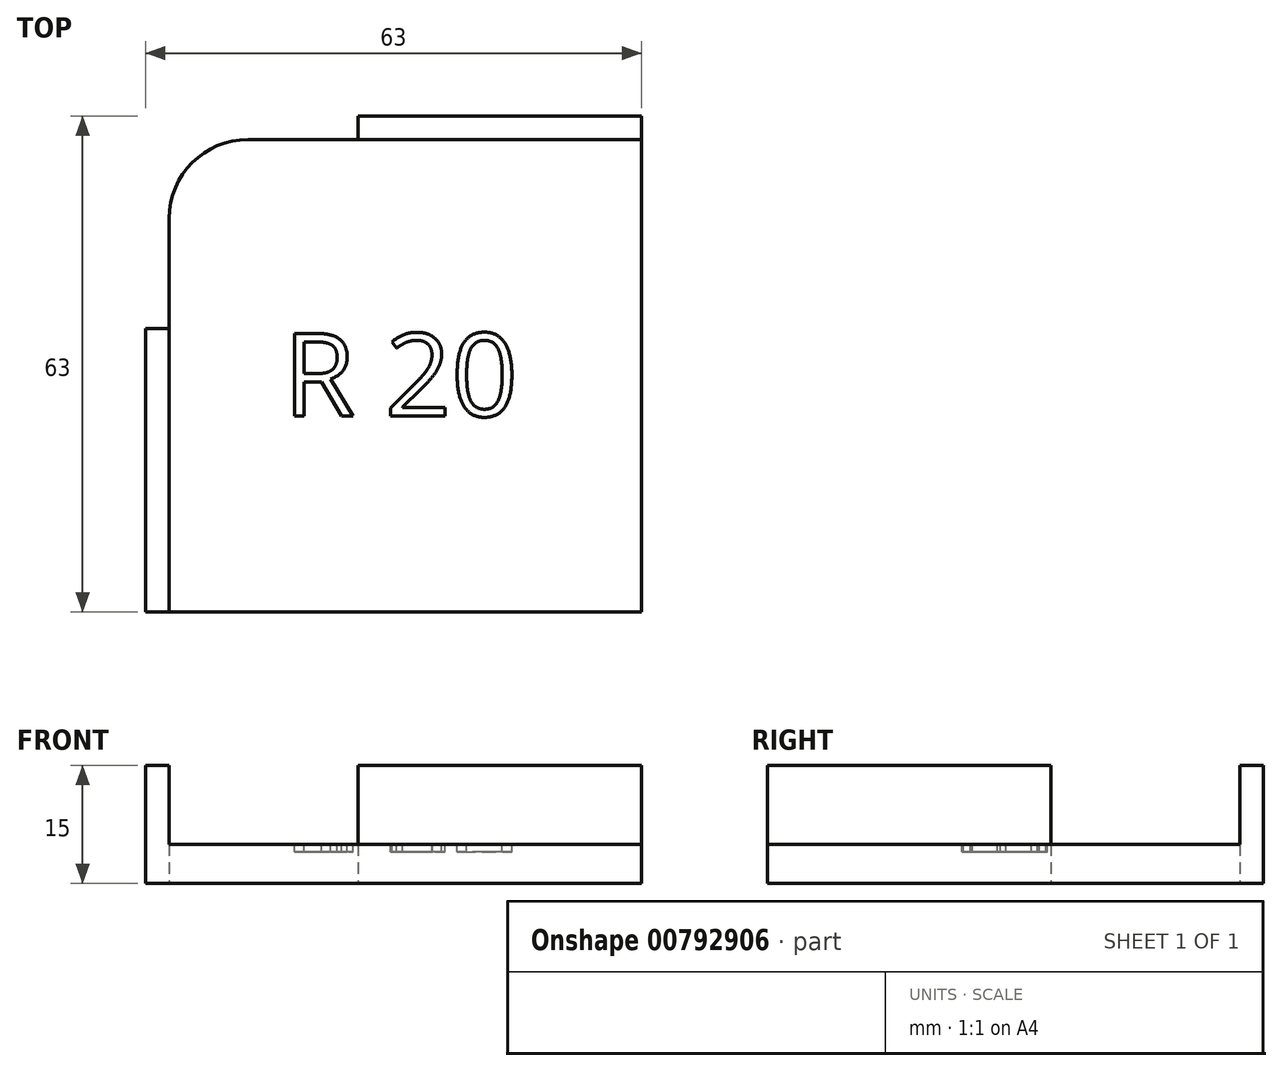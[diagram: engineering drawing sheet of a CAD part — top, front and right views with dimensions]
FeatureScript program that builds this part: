
annotation { "Feature Type Name" : "Feature", "Feature Type Description" : "" }
export const myFeature = defineFeature(function(context is Context, id is Id, definition is map)
    precondition{}
    {
        {
            var Q0;
            Q0=qCreatedBy(makeId("Top.planeOp"),FACE);
            var sketch = newSketch(context, id + "F0", { "sketchPlane" : qUnion([Q0])});
            skArc(sketch, "E0", {"start": v(0, 10) * mm, "mid": v(-7.07, 7.07) * mm, "end": v(-10, 0) * mm});
            skLineSegment(sketch, "E1", {"start": v(0, 10) * mm, "end": v(50, 10) * mm});
            skLineSegment(sketch, "E2", {"start": v(50, 10) * mm, "end": v(50, -50) * mm});
            skLineSegment(sketch, "E3", {"start": v(50, -50) * mm, "end": v(-10, -50) * mm});
            skLineSegment(sketch, "E4", {"start": v(-10, -50) * mm, "end": v(-10, 0) * mm});
            skSolve(sketch);
        }
        {
            var Q0;
            Q0 = qSketchRegion(id + "F0", true);
            extrude(context, id + "F1", {"entities" : qUnion([Q0]), "depth" : 5 * mm, "offsetDistance" : 25 * mm});
        }
        {
            var Q0;
            Q0=makeQuery(id+"F1.opExtrude","CAP_FACE",FACE,{"disambiguationData":[OSD([sQuery(id+"F0.wireOp",EDGE,"E0"),sQuery(id+"F0.wireOp",EDGE,"E1"),sQuery(id+"F0.wireOp",EDGE,"E2"),sQuery(id+"F0.wireOp",EDGE,"E3"),sQuery(id+"F0.wireOp",EDGE,"E4")])],"isStart":false});
            var sketch = newSketch(context, id + "F2", { "sketchPlane" : qUnion([Q0])});
            skLineSegment(sketch, "E5.bottom", {"start": v(-10, -50) * mm, "end": v(-13, -50) * mm});
            skLineSegment(sketch, "E5.top", {"start": v(-10, -14) * mm, "end": v(-13, -14) * mm});
            skLineSegment(sketch, "E5.left", {"start": v(-10, -50) * mm, "end": v(-10, -14) * mm});
            skLineSegment(sketch, "E5.right", {"start": v(-13, -50) * mm, "end": v(-13, -14) * mm});
            skLineSegment(sketch, "E6.bottom", {"start": v(50, 10) * mm, "end": v(14, 10) * mm});
            skLineSegment(sketch, "E6.top", {"start": v(50, 13) * mm, "end": v(14, 13) * mm});
            skLineSegment(sketch, "E6.left", {"start": v(50, 10) * mm, "end": v(50, 13) * mm});
            skLineSegment(sketch, "E6.right", {"start": v(14, 10) * mm, "end": v(14, 13) * mm});
            skSolve(sketch);
        }
        {
            var Q0;
            Q0 = qSketchRegion(id + "F2", true);
            var Q1;
            Q1=makeQuery(id+"F1.opExtrude","CAP_FACE",FACE,{"disambiguationData":[OSD([sQuery(id+"F0.wireOp",EDGE,"E0"),sQuery(id+"F0.wireOp",EDGE,"E1"),sQuery(id+"F0.wireOp",EDGE,"E2"),sQuery(id+"F0.wireOp",EDGE,"E3"),sQuery(id+"F0.wireOp",EDGE,"E4")])],"isStart":true});
            extrude(context, id + "F3", {"entities" : qUnion([Q0]), "operationType" : NewBodyOperationType.ADD, "depth" : 10 * mm, "offsetDistance" : 25 * mm, "hasSecondDirection" : true, "secondDirectionBound" : SecondDirectionBoundingType.UP_TO_SURFACE, "secondDirectionOppositeDirection" : true, "secondDirectionDepth" : 25 * mm, "secondDirectionBoundEntityFace" : qUnion([Q1])});
        }
        {
            var Q0;
            Q0=makeQuery(id+"F1.opExtrude","CAP_FACE",FACE,{"disambiguationData":[OSD([sQuery(id+"F0.wireOp",EDGE,"E0"),sQuery(id+"F0.wireOp",EDGE,"E1"),sQuery(id+"F0.wireOp",EDGE,"E2"),sQuery(id+"F0.wireOp",EDGE,"E3"),sQuery(id+"F0.wireOp",EDGE,"E4")])],"isStart":false});
            var sketch = newSketch(context, id + "F4", { "sketchPlane" : qUnion([Q0])});
            skText(sketch, "E7", { "text": "R 20", "fontName": "OpenSans-Regular.ttf"});
            const initialGuessF4  = {"E7": [0.00449, -0.02514, 1, 0, 0.0106]};
            skSetInitialGuess(sketch, initialGuessF4);
            skSolve(sketch);
        }
        {
            var Q0;
            Q0 = qSketchRegion(id + "F4", true);
            extrude(context, id + "F5", {"entities" : qUnion([Q0]), "operationType" : NewBodyOperationType.REMOVE, "oppositeDirection" : true, "depth" : 1 * mm, "offsetDistance" : 25 * mm});
        }
        {
            var Q0;
            Q0=makeQuery(id+"F1.opExtrude","SWEPT_BODY",BODY,{"disambiguationData":[OSD([sQuery(id+"F0.wireOp",EDGE,"E0"),sQuery(id+"F0.wireOp",EDGE,"E1"),sQuery(id+"F0.wireOp",EDGE,"E2"),sQuery(id+"F0.wireOp",EDGE,"E3"),sQuery(id+"F0.wireOp",EDGE,"E4")])]});
            transform(context, id + "F6", {"entities" : qUnion([Q0]), "transformType" : TransformType.TRANSLATION_3D, "dx" : 0 * mm, "dy" : 0 * mm, "dz" : 0 * mm, "makeCopy" : true});
        }
        {
            var Q0;
            Q0=makeQuery(id+"F1.opExtrude","SWEPT_BODY",BODY,{"disambiguationData":[OSD([sQuery(id+"F0.wireOp",EDGE,"E0"),sQuery(id+"F0.wireOp",EDGE,"E1"),sQuery(id+"F0.wireOp",EDGE,"E2"),sQuery(id+"F0.wireOp",EDGE,"E3"),sQuery(id+"F0.wireOp",EDGE,"E4")])]});
            deleteBodies(context, id + "F7", {"entities" : qUnion([Q0])});
        }
    });
